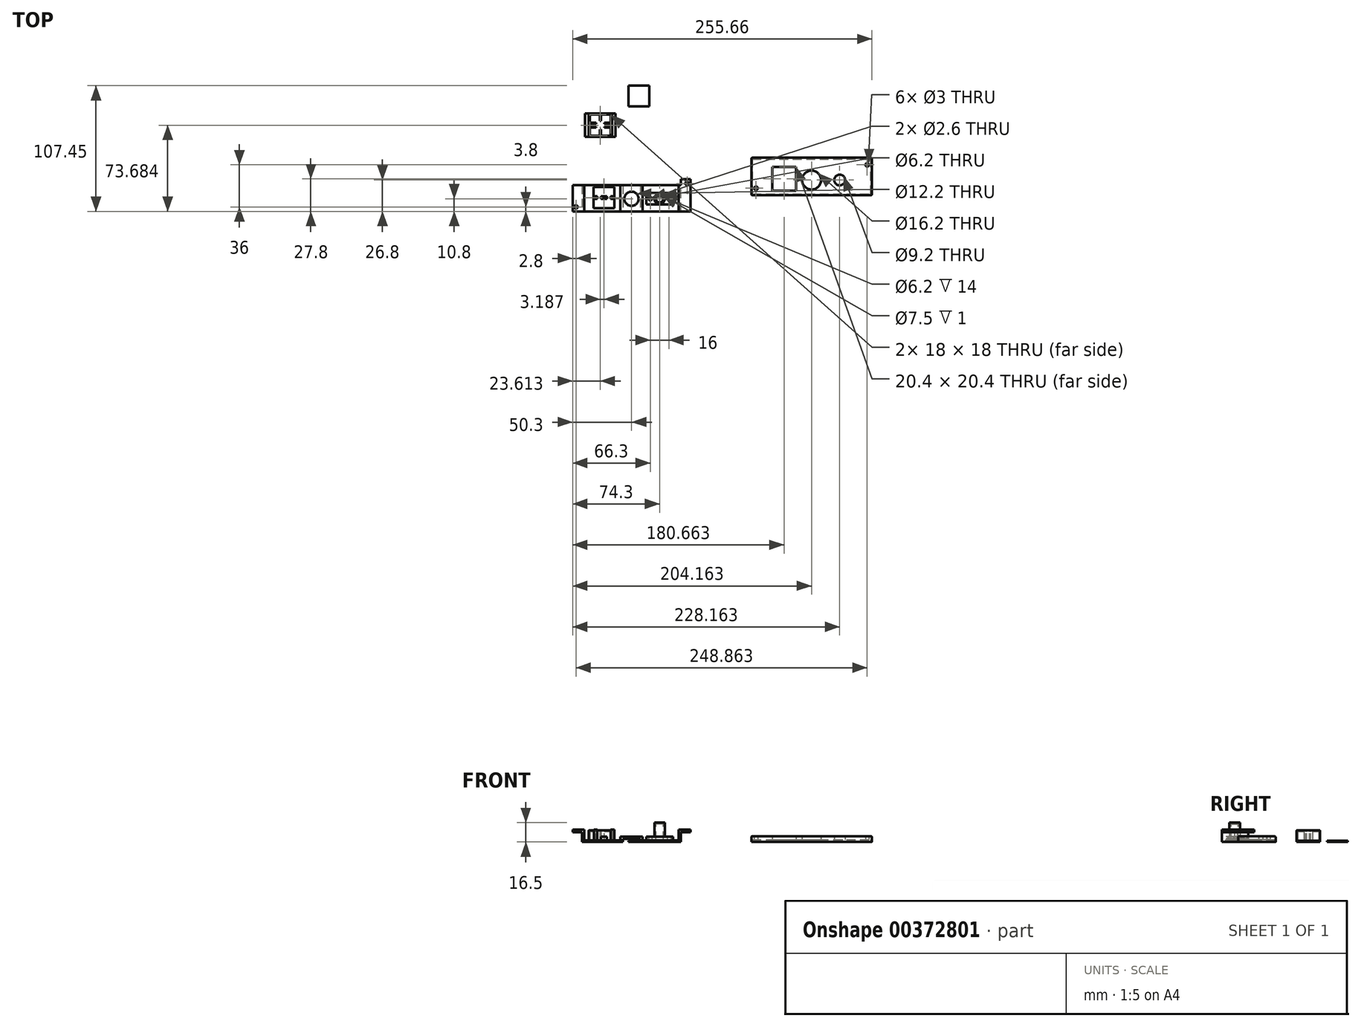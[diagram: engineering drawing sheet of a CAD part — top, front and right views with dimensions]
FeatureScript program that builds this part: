
annotation { "Feature Type Name" : "Feature", "Feature Type Description" : "" }
export const myFeature = defineFeature(function(context is Context, id is Id, definition is map)
    precondition{}
    {
        {
            var Q0;
            Q0=qCreatedBy(makeId("Top.planeOp"),FACE);
            var sketch = newSketch(context, id + "F0", { "sketchPlane" : qUnion([Q0])});
            skPoint(sketch, "E0.middle", {"position": v(0, 0) * mm});
            skCircle(sketch, "E1", {"center": v(-47.5, -10) * mm, "radius": 1.3 * mm, "construction": true});
            skCircle(sketch, "E2", {"center": v(47.5, 10) * mm, "radius": 1.3 * mm, "construction": true});
            skLineSegment(sketch, "E3.bottom", {"start": v(-32.5, 7) * mm, "end": v(-14.5, 7) * mm});
            skLineSegment(sketch, "E3.top", {"start": v(-32.5, -11) * mm, "end": v(-14.5, -11) * mm});
            skLineSegment(sketch, "E3.left", {"start": v(-32.5, 7) * mm, "end": v(-32.5, -1) * mm});
            skLineSegment(sketch, "E3.right", {"start": v(-14.5, 7) * mm, "end": v(-14.5, -11) * mm});
            skLineSegment(sketch, "E4.bottom", {"start": v(-29.25, 7) * mm, "end": v(-27.25, 7) * mm});
            skLineSegment(sketch, "E4.top", {"start": v(-29.25, -11) * mm, "end": v(-27.25, -11) * mm});
            skLineSegment(sketch, "E4.left", {"start": v(-29.25, 7) * mm, "end": v(-29.25, -1) * mm});
            skLineSegment(sketch, "E4.right", {"start": v(-27.25, 7) * mm, "end": v(-27.25, -1) * mm});
            skLineSegment(sketch, "E5.bottom", {"start": v(-19.75, 7) * mm, "end": v(-17.75, 7) * mm});
            skLineSegment(sketch, "E5.top", {"start": v(-19.75, -11) * mm, "end": v(-17.75, -11) * mm});
            skLineSegment(sketch, "E5.left", {"start": v(-19.75, 7) * mm, "end": v(-19.75, -1) * mm});
            skLineSegment(sketch, "E5.right", {"start": v(-17.75, 7) * mm, "end": v(-17.75, -1) * mm});
            skLineSegment(sketch, "E6.bottom", {"start": v(-32.5, -1) * mm, "end": v(-29.25, -1) * mm});
            skLineSegment(sketch, "E6.top", {"start": v(-32.5, -3) * mm, "end": v(-29.25, -3) * mm});
            skLineSegment(sketch, "E6.left", {"start": v(-32.5, -1) * mm, "end": v(-32.5, -3) * mm});
            skLineSegment(sketch, "E7.trimOffspring", {"start": v(-29.25, -3) * mm, "end": v(-29.25, -11) * mm});
            skLineSegment(sketch, "E8.trimOffspring", {"start": v(-27.25, -1) * mm, "end": v(-19.75, -1) * mm});
            skLineSegment(sketch, "E9.trimOffspring", {"start": v(-27.25, -3) * mm, "end": v(-27.25, -11) * mm});
            skLineSegment(sketch, "E10.trimOffspring", {"start": v(-27.25, -3) * mm, "end": v(-19.75, -3) * mm});
            skLineSegment(sketch, "E11.trimOffspring", {"start": v(-17.75, -1) * mm, "end": v(-14.5, -1) * mm});
            skLineSegment(sketch, "E12.trimOffspring", {"start": v(-17.75, -3) * mm, "end": v(-14.5, -3) * mm});
            skLineSegment(sketch, "E13.trimOffspring", {"start": v(-19.75, -3) * mm, "end": v(-19.75, -11) * mm});
            skLineSegment(sketch, "E14.trimOffspring", {"start": v(-17.75, -3) * mm, "end": v(-17.75, -11) * mm});
            skLineSegment(sketch, "E15.trimOffspring", {"start": v(-32.5, -3) * mm, "end": v(-32.5, -11) * mm});
            skCircle(sketch, "E16", {"center": v(24, -3) * mm, "radius": 3.1 * mm});
            skLineSegment(sketch, "E17.bottom", {"start": v(22.75, -10.5) * mm, "end": v(20.75, -10.5) * mm, "construction": true});
            skLineSegment(sketch, "E17.top", {"start": v(22.75, 4.5) * mm, "end": v(20.75, 4.5) * mm, "construction": true});
            skLineSegment(sketch, "E17.left", {"start": v(22.75, -10.5) * mm, "end": v(22.75, 4.5) * mm, "construction": true});
            skLineSegment(sketch, "E17.right", {"start": v(20.75, -10.5) * mm, "end": v(20.75, 4.5) * mm, "construction": true});
            skPoint(sketch, "E17.middle", {"position": v(21.75, -3) * mm});
            skLineSegment(sketch, "E18.bottom", {"start": v(25.25, -10.5) * mm, "end": v(27.25, -10.5) * mm, "construction": true});
            skLineSegment(sketch, "E18.top", {"start": v(25.25, 4.5) * mm, "end": v(27.25, 4.5) * mm, "construction": true});
            skLineSegment(sketch, "E18.left", {"start": v(25.25, -10.5) * mm, "end": v(25.25, 4.5) * mm, "construction": true});
            skLineSegment(sketch, "E18.right", {"start": v(27.25, -10.5) * mm, "end": v(27.25, 4.5) * mm, "construction": true});
            skPoint(sketch, "E18.middle", {"position": v(26.25, -3) * mm});
            skCircle(sketch, "E19", {"center": v(16, -3) * mm, "radius": 1.3 * mm});
            skPoint(sketch, "E19.centerSnap0", {"position": v(20.75, -3) * mm});
            skCircle(sketch, "E20", {"center": v(32, -3) * mm, "radius": 1.3 * mm});
            skPoint(sketch, "E20.centerSnap0", {"position": v(27.25, -3) * mm});
            skLineSegment(sketch, "E21.bottom", {"start": v(42.3, -13.8) * mm, "end": v(-42.3, -13.8) * mm});
            skLineSegment(sketch, "E21.top", {"start": v(42.3, 13.8) * mm, "end": v(-42.3, 13.8) * mm});
            skLineSegment(sketch, "E21.left", {"start": v(42.3, -13.8) * mm, "end": v(42.3, 13.8) * mm});
            skLineSegment(sketch, "E21.right", {"start": v(-42.3, -13.8) * mm, "end": v(-42.3, 13.8) * mm});
            skLineSegment(sketch, "E22.bottom", {"start": v(50.5, -15) * mm, "end": v(-50.5, -15) * mm, "construction": true});
            skLineSegment(sketch, "E22.top", {"start": v(50.5, 15) * mm, "end": v(-50.5, 15) * mm, "construction": true});
            skLineSegment(sketch, "E22.left", {"start": v(50.5, -15) * mm, "end": v(50.5, 15) * mm, "construction": true});
            skLineSegment(sketch, "E22.right", {"start": v(-50.5, -15) * mm, "end": v(-50.5, 15) * mm, "construction": true});
            skCircle(sketch, "E23", {"center": v(0, -3) * mm, "radius": 6.1 * mm, "construction": true});
            skSolve(sketch);
        }
        {
            var Q0;
            {var subQ9=sQuery(id+"F0.wireOp",EDGE,"E3.left");Q0=makeQuery(id+"F0.imprint","IMPRINT",FACE,{"disambiguationData":[TD([[makeQuery(id+"F0.imprint","IMPRINT",EDGE,{"derivedFrom":subQ9}),-1.0]])]});}
            var Q1;
            Q1=makeQuery(id+"F0.imprint","IMPRINT",FACE,{"disambiguationData":[TD([[makeQuery(id+"F0.imprint","IMPRINT",EDGE,{"derivedFrom":sQuery(id+"F0.wireOp",EDGE,"E4.bottom")}),-1.0]])]});
            extrude(context, id + "F1", {"entities" : qUnion([Q0, Q1]), "depth" : 1.5 * mm});
        }
        {
            var Q0;
            Q0=makeQuery(id+"F1.opExtrude","CAP_FACE",FACE,{"disambiguationData":[OSD([sQuery(id+"F0.wireOp",EDGE,"E1"),sQuery(id+"F0.wireOp",EDGE,"E2"),sQuery(id+"F0.wireOp",EDGE,"HjM1cqbq-AiCP-0QKJ-cJrE-Fvu34An3JJiY.bottom"),sQuery(id+"F0.wireOp",EDGE,"HjM1cqbq-AiCP-0QKJ-cJrE-Fvu34An3JJiY.top"),sQuery(id+"F0.wireOp",EDGE,"HjM1cqbq-AiCP-0QKJ-cJrE-Fvu34An3JJiY.left"),sQuery(id+"F0.wireOp",EDGE,"HjM1cqbq-AiCP-0QKJ-cJrE-Fvu34An3JJiY.right"),sQuery(id+"F0.wireOp",EDGE,"424KGZRB-5utR-a6Sk-f07y-1cyDiIB8TaRe"),sQuery(id+"F0.wireOp",EDGE,"xPdJMKwa-e6o6-zGCf-eMrl-vuys1Or93pA9"),sQuery(id+"F0.wireOp",EDGE,"E3.bottom"),sQuery(id+"F0.wireOp",EDGE,"E3.top"),sQuery(id+"F0.wireOp",EDGE,"E3.left"),sQuery(id+"F0.wireOp",EDGE,"E3.right"),sQuery(id+"F0.wireOp",EDGE,"E4.left"),sQuery(id+"F0.wireOp",EDGE,"E4.right"),sQuery(id+"F0.wireOp",EDGE,"E5.left"),sQuery(id+"F0.wireOp",EDGE,"E5.right"),sQuery(id+"F0.wireOp",EDGE,"E6.bottom"),sQuery(id+"F0.wireOp",EDGE,"E6.top"),sQuery(id+"F0.wireOp",EDGE,"E7.trimOffspring"),sQuery(id+"F0.wireOp",EDGE,"E8.trimOffspring"),sQuery(id+"F0.wireOp",EDGE,"E9.trimOffspring"),sQuery(id+"F0.wireOp",EDGE,"E10.trimOffspring"),sQuery(id+"F0.wireOp",EDGE,"E11.trimOffspring"),sQuery(id+"F0.wireOp",EDGE,"E12.trimOffspring"),sQuery(id+"F0.wireOp",EDGE,"E13.trimOffspring"),sQuery(id+"F0.wireOp",EDGE,"E14.trimOffspring"),sQuery(id+"F0.wireOp",EDGE,"E15.trimOffspring")])],"isStart":false});
            var sketch = newSketch(context, id + "F2", { "sketchPlane" : qUnion([Q0])});
            skLineSegment(sketch, "E24.bottom", {"start": v(-29.25, -1) * mm, "end": v(-32.25, -1) * mm});
            skLineSegment(sketch, "E24.top", {"start": v(-29.25, -3) * mm, "end": v(-32.25, -3) * mm});
            skLineSegment(sketch, "E24.left", {"start": v(-29.25, -1) * mm, "end": v(-29.25, -3) * mm});
            skLineSegment(sketch, "E24.right", {"start": v(-32.25, -1) * mm, "end": v(-32.25, -3) * mm});
            skLineSegment(sketch, "E25.bottom", {"start": v(-17.75, -1) * mm, "end": v(-14.75, -1) * mm});
            skLineSegment(sketch, "E25.top", {"start": v(-17.75, -3) * mm, "end": v(-14.75, -3) * mm});
            skLineSegment(sketch, "E25.left", {"start": v(-17.75, -1) * mm, "end": v(-17.75, -3) * mm});
            skLineSegment(sketch, "E25.right", {"start": v(-14.75, -1) * mm, "end": v(-14.75, -3) * mm});
            skSolve(sketch);
        }
        {
            var Q0;
            Q0=qSketchRegion(id+"F2",true);
            extrude(context, id + "F3", {"entities" : qUnion([Q0]), "operationType" : NewBodyOperationType.ADD, "depth" : 9 * mm});
        }
        {
            var Q0;
            Q0=qCreatedBy(makeId("Top.planeOp"),FACE);
            var sketch = newSketch(context, id + "F4", { "sketchPlane" : qUnion([Q0])});
            skLineSegment(sketch, "E26.bottom", {"start": v(-36.69, 69.88) * mm, "end": v(-16.69, 69.88) * mm});
            skLineSegment(sketch, "E26.top", {"start": v(-36.69, 49.88) * mm, "end": v(-16.69, 49.88) * mm});
            skLineSegment(sketch, "E26.left", {"start": v(-36.69, 69.88) * mm, "end": v(-36.69, 49.88) * mm});
            skLineSegment(sketch, "E26.right", {"start": v(-16.69, 69.88) * mm, "end": v(-16.69, 49.88) * mm});
            skLineSegment(sketch, "E27.bottom", {"start": v(-2.69, 93.65) * mm, "end": v(15.11, 93.65) * mm});
            skLineSegment(sketch, "E27.top", {"start": v(-2.69, 75.85) * mm, "end": v(15.11, 75.85) * mm});
            skLineSegment(sketch, "E27.left", {"start": v(-2.69, 93.65) * mm, "end": v(-2.69, 75.85) * mm});
            skLineSegment(sketch, "E27.right", {"start": v(15.11, 93.65) * mm, "end": v(15.11, 75.85) * mm});
            skSolve(sketch);
        }
        {
            var Q0;
            Q0=makeQuery(id+"F4.imprint","IMPRINT",FACE,{"disambiguationData":[TD([[makeQuery(id+"F4.imprint","IMPRINT",EDGE,{"derivedFrom":sQuery(id+"F4.wireOp",EDGE,"E26.bottom")}),-1.0]])]});
            extrude(context, id + "F5", {"entities" : qUnion([Q0]), "depth" : 10 * mm});
        }
        {
            var Q0;
            Q0=makeQuery(id+"F5.opExtrude","CAP_FACE",FACE,{"disambiguationData":[OSD([sQuery(id+"F4.wireOp",EDGE,"E26.bottom"),sQuery(id+"F4.wireOp",EDGE,"E26.top"),sQuery(id+"F4.wireOp",EDGE,"E26.left"),sQuery(id+"F4.wireOp",EDGE,"E26.right")])],"isStart":true});
            shell(context, id + "F6", {"entities" : qUnion([Q0]), "thickness" : 1 * mm});
        }
        {
            var Q0;
            Q0=makeQuery(id+"F5.opExtrude","CAP_FACE",FACE,{"disambiguationData":[OSD([sQuery(id+"F4.wireOp",EDGE,"E26.bottom"),sQuery(id+"F4.wireOp",EDGE,"E26.top"),sQuery(id+"F4.wireOp",EDGE,"E26.left"),sQuery(id+"F4.wireOp",EDGE,"E26.right")])],"isStart":true});
            var sketch = newSketch(context, id + "F7", { "sketchPlane" : qUnion([Q0])});
            skLineSegment(sketch, "E28.bottom", {"start": v(-35.69, -57.88) * mm, "end": v(-27.19, -57.88) * mm});
            skLineSegment(sketch, "E28.top", {"start": v(-35.69, -58.58) * mm, "end": v(-27.19, -58.58) * mm});
            skLineSegment(sketch, "E28.left", {"start": v(-35.69, -57.88) * mm, "end": v(-35.69, -58.58) * mm});
            skLineSegment(sketch, "E28.right", {"start": v(-17.69, -57.88) * mm, "end": v(-17.69, -58.58) * mm});
            skLineSegment(sketch, "E29.bottom", {"start": v(-35.69, -61.18) * mm, "end": v(-27.19, -61.18) * mm});
            skLineSegment(sketch, "E29.top", {"start": v(-35.69, -61.88) * mm, "end": v(-27.19, -61.88) * mm});
            skLineSegment(sketch, "E29.left", {"start": v(-35.69, -61.18) * mm, "end": v(-35.69, -61.88) * mm});
            skLineSegment(sketch, "E29.right", {"start": v(-17.69, -61.18) * mm, "end": v(-17.69, -61.88) * mm});
            skLineSegment(sketch, "E30.bottom", {"start": v(-27.19, -50.88) * mm, "end": v(-26.19, -50.88) * mm});
            skLineSegment(sketch, "E30.top", {"start": v(-27.19, -68.88) * mm, "end": v(-26.19, -68.88) * mm});
            skLineSegment(sketch, "E30.left", {"start": v(-27.19, -50.88) * mm, "end": v(-27.19, -68.88) * mm});
            skLineSegment(sketch, "E30.right", {"start": v(-26.19, -50.88) * mm, "end": v(-26.19, -68.88) * mm});
            skLineSegment(sketch, "E31.trimOffspring", {"start": v(-26.19, -57.88) * mm, "end": v(-17.69, -57.88) * mm});
            skLineSegment(sketch, "E32.trimOffspring", {"start": v(-26.19, -58.58) * mm, "end": v(-17.69, -58.58) * mm});
            skLineSegment(sketch, "E33.trimOffspring", {"start": v(-26.19, -61.18) * mm, "end": v(-17.69, -61.18) * mm});
            skLineSegment(sketch, "E34.trimOffspring", {"start": v(-26.19, -61.88) * mm, "end": v(-17.69, -61.88) * mm});
            skSolve(sketch);
        }
        {
            var Q0;
            Q0=qSketchRegion(id+"F7",true);
            extrude(context, id + "F8", {"entities" : qUnion([Q0]), "operationType" : NewBodyOperationType.ADD, "oppositeDirection" : true, "depth" : 9 * mm});
        }
        {
            var Q0;
            Q0=makeQuery(id+"F8.boolean.opBoolean","MERGE",FACE,{"derivedFrom":[makeQuery(id+"F5.opExtrude","CAP_FACE",FACE,{"disambiguationData":[OSD([sQuery(id+"F4.wireOp",EDGE,"E26.bottom"),sQuery(id+"F4.wireOp",EDGE,"E26.top"),sQuery(id+"F4.wireOp",EDGE,"E26.left"),sQuery(id+"F4.wireOp",EDGE,"E26.right")])],"isStart":true}),makeQuery(id+"F8.opExtrude","CAP_FACE",FACE,{"disambiguationData":[OSD([sQuery(id+"F7.wireOp",EDGE,"E28.bottom"),sQuery(id+"F7.wireOp",EDGE,"E28.top"),sQuery(id+"F7.wireOp",EDGE,"E28.left"),sQuery(id+"F7.wireOp",EDGE,"E28.right"),sQuery(id+"F7.wireOp",EDGE,"E29.bottom"),sQuery(id+"F7.wireOp",EDGE,"E29.top"),sQuery(id+"F7.wireOp",EDGE,"E29.left"),sQuery(id+"F7.wireOp",EDGE,"E29.right"),sQuery(id+"F7.wireOp",EDGE,"E30.bottom"),sQuery(id+"F7.wireOp",EDGE,"E30.top"),sQuery(id+"F7.wireOp",EDGE,"E30.left"),sQuery(id+"F7.wireOp",EDGE,"E30.right"),sQuery(id+"F7.wireOp",EDGE,"E31.trimOffspring"),sQuery(id+"F7.wireOp",EDGE,"E32.trimOffspring"),sQuery(id+"F7.wireOp",EDGE,"E33.trimOffspring"),sQuery(id+"F7.wireOp",EDGE,"E34.trimOffspring")])],"isStart":true})]});
            var sketch = newSketch(context, id + "F9", { "sketchPlane" : qUnion([Q0])});
            skLineSegment(sketch, "E35.bottom", {"start": v(-30.29, -56.28) * mm, "end": v(-23.09, -56.28) * mm});
            skLineSegment(sketch, "E35.top", {"start": v(-30.29, -63.48) * mm, "end": v(-23.09, -63.48) * mm});
            skLineSegment(sketch, "E35.left", {"start": v(-30.29, -56.28) * mm, "end": v(-30.29, -63.48) * mm});
            skLineSegment(sketch, "E35.right", {"start": v(-23.09, -56.28) * mm, "end": v(-23.09, -63.48) * mm});
            skSolve(sketch);
        }
        {
            var Q0;
            Q0=qSketchRegion(id+"F9",true);
            extrude(context, id + "F10", {"entities" : qUnion([Q0]), "operationType" : NewBodyOperationType.REMOVE, "oppositeDirection" : true, "depth" : 9 * mm});
        }
        {
            var Q0;
            Q0=makeQuery(id+"F8.boolean.opBoolean","MERGE",FACE,{"derivedFrom":[makeQuery(id+"F5.opExtrude","CAP_FACE",FACE,{"disambiguationData":[OSD([sQuery(id+"F4.wireOp",EDGE,"E26.bottom"),sQuery(id+"F4.wireOp",EDGE,"E26.top"),sQuery(id+"F4.wireOp",EDGE,"E26.left"),sQuery(id+"F4.wireOp",EDGE,"E26.right")])],"isStart":true}),makeQuery(id+"F8.opExtrude","CAP_FACE",FACE,{"disambiguationData":[OSD([sQuery(id+"F7.wireOp",EDGE,"E28.bottom"),sQuery(id+"F7.wireOp",EDGE,"E28.top"),sQuery(id+"F7.wireOp",EDGE,"E28.left"),sQuery(id+"F7.wireOp",EDGE,"E28.right"),sQuery(id+"F7.wireOp",EDGE,"E29.bottom"),sQuery(id+"F7.wireOp",EDGE,"E29.top"),sQuery(id+"F7.wireOp",EDGE,"E29.left"),sQuery(id+"F7.wireOp",EDGE,"E29.right"),sQuery(id+"F7.wireOp",EDGE,"E30.bottom"),sQuery(id+"F7.wireOp",EDGE,"E30.top"),sQuery(id+"F7.wireOp",EDGE,"E30.left"),sQuery(id+"F7.wireOp",EDGE,"E30.right"),sQuery(id+"F7.wireOp",EDGE,"E31.trimOffspring"),sQuery(id+"F7.wireOp",EDGE,"E32.trimOffspring"),sQuery(id+"F7.wireOp",EDGE,"E33.trimOffspring"),sQuery(id+"F7.wireOp",EDGE,"E34.trimOffspring")])],"isStart":true})]});
            var sketch = newSketch(context, id + "F11", { "sketchPlane" : qUnion([Q0])});
            skLineSegment(sketch, "E36.bottom", {"start": v(-16.69, -69.88) * mm, "end": v(-13.69, -69.88) * mm});
            skLineSegment(sketch, "E36.top", {"start": v(-16.69, -49.88) * mm, "end": v(-13.69, -49.88) * mm});
            skLineSegment(sketch, "E36.left", {"start": v(-16.69, -69.88) * mm, "end": v(-16.69, -49.88) * mm});
            skLineSegment(sketch, "E36.right", {"start": v(-13.69, -69.88) * mm, "end": v(-13.69, -49.88) * mm});
            skLineSegment(sketch, "E37.bottom", {"start": v(-36.69, -69.88) * mm, "end": v(-39.69, -69.88) * mm});
            skLineSegment(sketch, "E37.top", {"start": v(-36.69, -49.88) * mm, "end": v(-39.69, -49.88) * mm});
            skLineSegment(sketch, "E37.left", {"start": v(-36.69, -69.88) * mm, "end": v(-36.69, -49.88) * mm});
            skLineSegment(sketch, "E37.right", {"start": v(-39.69, -69.88) * mm, "end": v(-39.69, -49.88) * mm});
            skSolve(sketch);
        }
        {
            var Q0;
            Q0=makeQuery(id+"F11.imprint","IMPRINT",FACE,{"disambiguationData":[TD([[makeQuery(id+"F11.imprint","IMPRINT",EDGE,{"derivedFrom":sQuery(id+"F11.wireOp",EDGE,"E37.bottom")}),-1.0]])]});
            var Q1;
            Q1=makeQuery(id+"F11.imprint","IMPRINT",FACE,{"disambiguationData":[TD([[makeQuery(id+"F11.imprint","IMPRINT",EDGE,{"derivedFrom":sQuery(id+"F11.wireOp",EDGE,"E36.bottom")}),1.0]])]});
            extrude(context, id + "F12", {"entities" : qUnion([Q0, Q1]), "operationType" : NewBodyOperationType.ADD, "oppositeDirection" : true, "depth" : 1 * mm});
        }
        {
            var Q0;
            Q0=makeQuery(id+"F5.opExtrude","CAP_FACE",FACE,{"disambiguationData":[OSD([sQuery(id+"F4.wireOp",EDGE,"E26.bottom"),sQuery(id+"F4.wireOp",EDGE,"E26.top"),sQuery(id+"F4.wireOp",EDGE,"E26.left"),sQuery(id+"F4.wireOp",EDGE,"E26.right")])],"isStart":false});
            var sketch = newSketch(context, id + "F13", { "sketchPlane" : qUnion([Q0])});
            skLineSegment(sketch, "E38.bottom", {"start": v(-35.69, 68.88) * mm, "end": v(-17.69, 68.88) * mm});
            skLineSegment(sketch, "E38.top", {"start": v(-35.69, 50.88) * mm, "end": v(-17.69, 50.88) * mm});
            skLineSegment(sketch, "E38.left", {"start": v(-35.69, 68.88) * mm, "end": v(-35.69, 50.88) * mm});
            skLineSegment(sketch, "E38.right", {"start": v(-17.69, 68.88) * mm, "end": v(-17.69, 50.88) * mm});
            skSolve(sketch);
        }
        {
            var Q0;
            Q0=qSketchRegion(id+"F13",true);
            extrude(context, id + "F14", {"entities" : qUnion([Q0]), "operationType" : NewBodyOperationType.REMOVE, "oppositeDirection" : true, "depth" : 1 * mm});
        }
        {
            var Q0;
            Q0=makeQuery(id+"F5.opExtrude","SWEPT_EDGE",EDGE,{"disambiguationData":[OSD([sQuery(id+"F4.wireOp",EDGE,"E26.top"),sQuery(id+"F4.wireOp",EDGE,"E26.right")])]});
            var Q1;
            Q1=makeQuery(id+"F5.opExtrude","SWEPT_EDGE",EDGE,{"disambiguationData":[OSD([sQuery(id+"F4.wireOp",EDGE,"E26.bottom"),sQuery(id+"F4.wireOp",EDGE,"E26.right")])]});
            var Q2;
            Q2=makeQuery(id+"F5.opExtrude","CAP_EDGE",EDGE,{"disambiguationData":[OSD([sQuery(id+"F4.wireOp",EDGE,"E26.right")])],"isStart":false});
            var Q3;
            Q3=makeQuery(id+"F5.opExtrude","CAP_EDGE",EDGE,{"disambiguationData":[OSD([sQuery(id+"F4.wireOp",EDGE,"E26.bottom")])],"isStart":false});
            var Q4;
            Q4=makeQuery(id+"F5.opExtrude","CAP_EDGE",EDGE,{"disambiguationData":[OSD([sQuery(id+"F4.wireOp",EDGE,"E26.top")])],"isStart":false});
            var Q5;
            Q5=makeQuery(id+"F5.opExtrude","CAP_EDGE",EDGE,{"disambiguationData":[OSD([sQuery(id+"F4.wireOp",EDGE,"E26.left")])],"isStart":false});
            var Q6;
            Q6=makeQuery(id+"F5.opExtrude","SWEPT_EDGE",EDGE,{"disambiguationData":[OSD([sQuery(id+"F4.wireOp",EDGE,"E26.top"),sQuery(id+"F4.wireOp",EDGE,"E26.left")])]});
            var Q7;
            Q7=makeQuery(id+"F5.opExtrude","SWEPT_EDGE",EDGE,{"disambiguationData":[OSD([sQuery(id+"F4.wireOp",EDGE,"E26.bottom"),sQuery(id+"F4.wireOp",EDGE,"E26.left")])]});
            fillet(context, id + "F15", {"entities" : qUnion([Q0, Q1, Q2, Q3, Q4, Q5, Q6, Q7]), "radius" : 0.5 * mm, "tangentPropagation" : true, "allowEdgeOverflow" : false});
        }
        {
            var Q0;
            Q0=makeQuery(id+"F4.imprint","IMPRINT",FACE,{"disambiguationData":[TD([[makeQuery(id+"F4.imprint","IMPRINT",EDGE,{"derivedFrom":sQuery(id+"F4.wireOp",EDGE,"E27.bottom")}),-1.0]])]});
            extrude(context, id + "F16", {"entities" : qUnion([Q0]), "depth" : 1 * mm});
        }
        {
            var Q0;
            Q0=makeQuery(id+"F1.opExtrude","CAP_FACE",FACE,{"disambiguationData":[OSD([sQuery(id+"F0.wireOp",EDGE,"E1"),sQuery(id+"F0.wireOp",EDGE,"E2"),sQuery(id+"F0.wireOp",EDGE,"HjM1cqbq-AiCP-0QKJ-cJrE-Fvu34An3JJiY.bottom"),sQuery(id+"F0.wireOp",EDGE,"HjM1cqbq-AiCP-0QKJ-cJrE-Fvu34An3JJiY.top"),sQuery(id+"F0.wireOp",EDGE,"HjM1cqbq-AiCP-0QKJ-cJrE-Fvu34An3JJiY.left"),sQuery(id+"F0.wireOp",EDGE,"HjM1cqbq-AiCP-0QKJ-cJrE-Fvu34An3JJiY.right"),sQuery(id+"F0.wireOp",EDGE,"424KGZRB-5utR-a6Sk-f07y-1cyDiIB8TaRe"),sQuery(id+"F0.wireOp",EDGE,"xPdJMKwa-e6o6-zGCf-eMrl-vuys1Or93pA9"),sQuery(id+"F0.wireOp",EDGE,"E3.bottom"),sQuery(id+"F0.wireOp",EDGE,"E3.top"),sQuery(id+"F0.wireOp",EDGE,"E3.left"),sQuery(id+"F0.wireOp",EDGE,"E3.right"),sQuery(id+"F0.wireOp",EDGE,"E4.left"),sQuery(id+"F0.wireOp",EDGE,"E4.right"),sQuery(id+"F0.wireOp",EDGE,"E5.left"),sQuery(id+"F0.wireOp",EDGE,"E5.right"),sQuery(id+"F0.wireOp",EDGE,"E6.bottom"),sQuery(id+"F0.wireOp",EDGE,"E6.top"),sQuery(id+"F0.wireOp",EDGE,"E7.trimOffspring"),sQuery(id+"F0.wireOp",EDGE,"E8.trimOffspring"),sQuery(id+"F0.wireOp",EDGE,"E9.trimOffspring"),sQuery(id+"F0.wireOp",EDGE,"E10.trimOffspring"),sQuery(id+"F0.wireOp",EDGE,"E11.trimOffspring"),sQuery(id+"F0.wireOp",EDGE,"E12.trimOffspring"),sQuery(id+"F0.wireOp",EDGE,"E13.trimOffspring"),sQuery(id+"F0.wireOp",EDGE,"E14.trimOffspring"),sQuery(id+"F0.wireOp",EDGE,"E15.trimOffspring")])],"isStart":false});
            var sketch = newSketch(context, id + "F17", { "sketchPlane" : qUnion([Q0])});
            skLineSegment(sketch, "E39.bottom", {"start": v(-26, -1) * mm, "end": v(-21, -1) * mm});
            skLineSegment(sketch, "E39.top", {"start": v(-26, -3) * mm, "end": v(-21, -3) * mm});
            skLineSegment(sketch, "E39.left", {"start": v(-26, -1) * mm, "end": v(-26, -3) * mm});
            skLineSegment(sketch, "E39.right", {"start": v(-21, -1) * mm, "end": v(-21, -3) * mm});
            skSolve(sketch);
        }
        {
            var Q0;
            Q0=qSketchRegion(id+"F17",true);
            extrude(context, id + "F18", {"entities" : qUnion([Q0]), "operationType" : NewBodyOperationType.ADD, "depth" : 3 * mm});
        }
        {
            var Q0;
            Q0=qCreatedBy(makeId("Top.planeOp"),FACE);
            var sketch = newSketch(context, id + "F19", { "sketchPlane" : qUnion([Q0])});
            skLineSegment(sketch, "E40.bottom", {"start": v(103.36, 32) * mm, "end": v(204.36, 32) * mm, "construction": true});
            skLineSegment(sketch, "E40.top", {"start": v(103.36, 0) * mm, "end": v(204.36, 0) * mm, "construction": true});
            skLineSegment(sketch, "E40.left", {"start": v(103.36, 32) * mm, "end": v(103.36, 0) * mm, "construction": true});
            skLineSegment(sketch, "E40.right", {"start": v(204.36, 32) * mm, "end": v(204.36, 0) * mm, "construction": true});
            skLineSegment(sketch, "E41.bottom", {"start": v(102.36, 32) * mm, "end": v(205.36, 32) * mm});
            skLineSegment(sketch, "E41.top", {"start": v(102.36, 0) * mm, "end": v(205.36, 0) * mm});
            skLineSegment(sketch, "E41.left", {"start": v(102.36, 32) * mm, "end": v(102.36, 0) * mm});
            skLineSegment(sketch, "E41.right", {"start": v(205.36, 32) * mm, "end": v(205.36, 0) * mm});
            skCircle(sketch, "E42", {"center": v(106.36, 6) * mm, "radius": 1.5 * mm});
            skCircle(sketch, "E43", {"center": v(201.36, 26) * mm, "radius": 1.5 * mm});
            skCircle(sketch, "E44", {"center": v(153.86, 13) * mm, "radius": 8.1 * mm});
            skCircle(sketch, "E45", {"center": v(177.86, 13) * mm, "radius": 4.6 * mm});
            skLineSegment(sketch, "E46.bottom", {"start": v(140.56, 3.8) * mm, "end": v(120.16, 3.8) * mm});
            skLineSegment(sketch, "E46.top", {"start": v(140.56, 24.2) * mm, "end": v(120.16, 24.2) * mm});
            skLineSegment(sketch, "E46.left", {"start": v(140.56, 3.8) * mm, "end": v(140.56, 24.2) * mm});
            skLineSegment(sketch, "E46.right", {"start": v(120.16, 3.8) * mm, "end": v(120.16, 24.2) * mm});
            skPoint(sketch, "E46.middle", {"position": v(130.36, 14) * mm});
            skSolve(sketch);
        }
        {
            var Q0;
            Q0=qSketchRegion(id+"F19",true);
            extrude(context, id + "F20", {"entities" : qUnion([Q0]), "depth" : 5 * mm});
        }
        {
            var Q0;
            Q0=makeQuery(id+"F20.opExtrude","CAP_FACE",FACE,{"disambiguationData":[OSD([sQuery(id+"F19.wireOp",EDGE,"E41.bottom"),sQuery(id+"F19.wireOp",EDGE,"E41.top"),sQuery(id+"F19.wireOp",EDGE,"E41.left"),sQuery(id+"F19.wireOp",EDGE,"E41.right"),sQuery(id+"F19.wireOp",EDGE,"E42"),sQuery(id+"F19.wireOp",EDGE,"E43"),sQuery(id+"F19.wireOp",EDGE,"RyGLUrYX-1u43-e16M-MsOJ-A2O3aQofN9jR.bottom"),sQuery(id+"F19.wireOp",EDGE,"RyGLUrYX-1u43-e16M-MsOJ-A2O3aQofN9jR.top"),sQuery(id+"F19.wireOp",EDGE,"RyGLUrYX-1u43-e16M-MsOJ-A2O3aQofN9jR.left"),sQuery(id+"F19.wireOp",EDGE,"RyGLUrYX-1u43-e16M-MsOJ-A2O3aQofN9jR.right")])],"isStart":true});
            var sketch = newSketch(context, id + "F21", { "sketchPlane" : qUnion([Q0])});
            skLineSegment(sketch, "E47.bottom", {"start": v(103.36, -1) * mm, "end": v(204.36, -1) * mm});
            skLineSegment(sketch, "E47.top", {"start": v(103.36, -31) * mm, "end": v(204.36, -31) * mm});
            skLineSegment(sketch, "E47.left", {"start": v(103.36, -1) * mm, "end": v(103.36, -31) * mm});
            skLineSegment(sketch, "E47.right", {"start": v(204.36, -1) * mm, "end": v(204.36, -31) * mm});
            skSolve(sketch);
        }
        {
            var Q0;
            Q0=qSketchRegion(id+"F21",true);
            extrude(context, id + "F22", {"entities" : qUnion([Q0]), "operationType" : NewBodyOperationType.REMOVE, "oppositeDirection" : true, "depth" : 2 * mm});
        }
        {
            var Q0;
            Q0=makeQuery(id+"F20.opExtrude","CAP_EDGE",EDGE,{"disambiguationData":[OSD([sQuery(id+"F19.wireOp",EDGE,"E41.left")])],"isStart":false});
            var Q1;
            Q1=makeQuery(id+"F20.opExtrude","CAP_EDGE",EDGE,{"disambiguationData":[OSD([sQuery(id+"F19.wireOp",EDGE,"E41.bottom")])],"isStart":false});
            var Q2;
            Q2=makeQuery(id+"F20.opExtrude","CAP_EDGE",EDGE,{"disambiguationData":[OSD([sQuery(id+"F19.wireOp",EDGE,"E41.top")])],"isStart":false});
            var Q3;
            Q3=makeQuery(id+"F20.opExtrude","CAP_EDGE",EDGE,{"disambiguationData":[OSD([sQuery(id+"F19.wireOp",EDGE,"E41.right")])],"isStart":false});
            var Q4;
            Q4=makeQuery(id+"F20.opExtrude","SWEPT_EDGE",EDGE,{"disambiguationData":[OSD([sQuery(id+"F19.wireOp",EDGE,"E41.bottom"),sQuery(id+"F19.wireOp",EDGE,"E41.right")])]});
            var Q5;
            Q5=makeQuery(id+"F20.opExtrude","SWEPT_EDGE",EDGE,{"disambiguationData":[OSD([sQuery(id+"F19.wireOp",EDGE,"E41.top"),sQuery(id+"F19.wireOp",EDGE,"E41.right")])]});
            var Q6;
            Q6=makeQuery(id+"F20.opExtrude","SWEPT_EDGE",EDGE,{"disambiguationData":[OSD([sQuery(id+"F19.wireOp",EDGE,"E41.bottom"),sQuery(id+"F19.wireOp",EDGE,"E41.left")])]});
            var Q7;
            Q7=makeQuery(id+"F20.opExtrude","SWEPT_EDGE",EDGE,{"disambiguationData":[OSD([sQuery(id+"F19.wireOp",EDGE,"E41.top"),sQuery(id+"F19.wireOp",EDGE,"E41.left")])]});
            fillet(context, id + "F23", {"entities" : qUnion([Q0, Q1, Q2, Q3, Q4, Q5, Q6, Q7]), "radius" : 1 * mm, "tangentPropagation" : true, "allowEdgeOverflow" : false});
        }
        {
            var Q0;
            Q0=makeQuery(id+"F1.opExtrude","SWEPT_FACE",FACE,{"disambiguationData":[OSD([sQuery(id+"F0.wireOp",EDGE,"E21.bottom")])]});
            var sketch = newSketch(context, id + "F24", { "sketchPlane" : qUnion([Q0])});
            skLineSegment(sketch, "E48.bottom", {"start": v(-42.3, 1.5) * mm, "end": v(-40.3, 1.5) * mm});
            skLineSegment(sketch, "E48.left", {"start": v(-42.3, 1.5) * mm, "end": v(-42.3, 8.5) * mm});
            skLineSegment(sketch, "E48.right", {"start": v(-40.3, 1.5) * mm, "end": v(-40.3, 10.5) * mm});
            skLineSegment(sketch, "E49.bottom", {"start": v(-40.3, 10.5) * mm, "end": v(-50.3, 10.5) * mm});
            skLineSegment(sketch, "E49.top", {"start": v(-42.3, 8.5) * mm, "end": v(-50.3, 8.5) * mm});
            skLineSegment(sketch, "E49.right", {"start": v(-50.3, 10.5) * mm, "end": v(-50.3, 8.5) * mm});
            skLineSegment(sketch, "E50", {"start": v(0, 8.22) * mm, "end": v(0, -6.23) * mm, "construction": true});
            skPoint(sketch, "E50.endSnap0", {"position": v(0, 1.5) * mm});
            skLineSegment(sketch, "E51.MirrorCS", {"start": v(42.3, 10.5) * mm, "end": v(40.3, 10.5) * mm});
            skLineSegment(sketch, "E52.MirrorCS", {"start": v(42.3, 10.5) * mm, "end": v(42.3, 8.5) * mm});
            skLineSegment(sketch, "E53.MirrorCS", {"start": v(42.3, 1.5) * mm, "end": v(40.3, 1.5) * mm});
            skLineSegment(sketch, "E54.MirrorCS", {"start": v(40.3, 1.5) * mm, "end": v(40.3, 10.5) * mm});
            skLineSegment(sketch, "E55.MirrorCS", {"start": v(50.3, 10.5) * mm, "end": v(50.3, 8.5) * mm});
            skLineSegment(sketch, "E56.MirrorCS", {"start": v(42.3, 1.5) * mm, "end": v(42.3, 10.5) * mm});
            skLineSegment(sketch, "E57.MirrorCS", {"start": v(42.3, 10.5) * mm, "end": v(50.3, 10.5) * mm});
            skLineSegment(sketch, "E58.MirrorCS", {"start": v(42.3, 8.5) * mm, "end": v(50.3, 8.5) * mm});
            skSolve(sketch);
        }
        {
            var Q0;
            Q0=qSketchRegion(id+"F24",true);
            extrude(context, id + "F25", {"entities" : qUnion([Q0]), "operationType" : NewBodyOperationType.ADD, "oppositeDirection" : true, "depth" : 27.6 * mm});
        }
        {
            var Q0;
            Q0=sQuery(id+"F0.wireOp",VERTEX,"E1.center");
            var Q1;
            Q1=sQuery(id+"F0.wireOp",VERTEX,"E2.center");
            var Q2;
            Q2=makeQuery(id+"F1.opExtrude","SWEPT_BODY",BODY,{"disambiguationData":[OSD([sQuery(id+"F0.wireOp",EDGE,"E3.bottom"),sQuery(id+"F0.wireOp",EDGE,"E3.top"),sQuery(id+"F0.wireOp",EDGE,"E3.left"),sQuery(id+"F0.wireOp",EDGE,"E3.right"),sQuery(id+"F0.wireOp",EDGE,"E4.left"),sQuery(id+"F0.wireOp",EDGE,"E4.right"),sQuery(id+"F0.wireOp",EDGE,"E5.left"),sQuery(id+"F0.wireOp",EDGE,"E5.right"),sQuery(id+"F0.wireOp",EDGE,"E6.bottom"),sQuery(id+"F0.wireOp",EDGE,"E6.top"),sQuery(id+"F0.wireOp",EDGE,"E7.trimOffspring"),sQuery(id+"F0.wireOp",EDGE,"E8.trimOffspring"),sQuery(id+"F0.wireOp",EDGE,"E9.trimOffspring"),sQuery(id+"F0.wireOp",EDGE,"E10.trimOffspring"),sQuery(id+"F0.wireOp",EDGE,"E11.trimOffspring"),sQuery(id+"F0.wireOp",EDGE,"E12.trimOffspring"),sQuery(id+"F0.wireOp",EDGE,"E13.trimOffspring"),sQuery(id+"F0.wireOp",EDGE,"E14.trimOffspring"),sQuery(id+"F0.wireOp",EDGE,"E15.trimOffspring"),sQuery(id+"F0.wireOp",EDGE,"E17.bottom"),sQuery(id+"F0.wireOp",EDGE,"E17.top"),sQuery(id+"F0.wireOp",EDGE,"E17.left"),sQuery(id+"F0.wireOp",EDGE,"E17.right"),sQuery(id+"F0.wireOp",EDGE,"E18.bottom"),sQuery(id+"F0.wireOp",EDGE,"E18.top"),sQuery(id+"F0.wireOp",EDGE,"E18.left"),sQuery(id+"F0.wireOp",EDGE,"E18.right"),sQuery(id+"F0.wireOp",EDGE,"E19"),sQuery(id+"F0.wireOp",EDGE,"E20"),sQuery(id+"F0.wireOp",EDGE,"E21.bottom"),sQuery(id+"F0.wireOp",EDGE,"E21.top"),sQuery(id+"F0.wireOp",EDGE,"E21.left"),sQuery(id+"F0.wireOp",EDGE,"E21.right"),sQuery(id+"F0.wireOp",EDGE,"P8dx2Xio-yyFz-oP8E-liUG-BQfSMQLC5rHF")])]});
            hole(context, id + "F26", {"style" : HoleStyle.SIMPLE, "endStyle" : HoleEndStyle.BLIND, "oppositeDirection" : true, "holeDiameter" : 3 * mm, "holeDepth" : 5 * mm, "tappedDepth" : 12 * mm, "tapClearance" : 3, "locations" : qUnion([Q0, Q1]), "scope" : qUnion([Q2])});
        }
        {
            var Q0;
            Q0=makeQuery(id+"F1.opExtrude","CAP_FACE",FACE,{"disambiguationData":[OSD([sQuery(id+"F0.wireOp",EDGE,"E3.bottom"),sQuery(id+"F0.wireOp",EDGE,"E3.top"),sQuery(id+"F0.wireOp",EDGE,"E3.left"),sQuery(id+"F0.wireOp",EDGE,"E3.right"),sQuery(id+"F0.wireOp",EDGE,"E4.left"),sQuery(id+"F0.wireOp",EDGE,"E4.right"),sQuery(id+"F0.wireOp",EDGE,"E5.left"),sQuery(id+"F0.wireOp",EDGE,"E5.right"),sQuery(id+"F0.wireOp",EDGE,"E6.bottom"),sQuery(id+"F0.wireOp",EDGE,"E6.top"),sQuery(id+"F0.wireOp",EDGE,"E7.trimOffspring"),sQuery(id+"F0.wireOp",EDGE,"E8.trimOffspring"),sQuery(id+"F0.wireOp",EDGE,"E9.trimOffspring"),sQuery(id+"F0.wireOp",EDGE,"E10.trimOffspring"),sQuery(id+"F0.wireOp",EDGE,"E11.trimOffspring"),sQuery(id+"F0.wireOp",EDGE,"E12.trimOffspring"),sQuery(id+"F0.wireOp",EDGE,"E13.trimOffspring"),sQuery(id+"F0.wireOp",EDGE,"E14.trimOffspring"),sQuery(id+"F0.wireOp",EDGE,"E15.trimOffspring"),sQuery(id+"F0.wireOp",EDGE,"E17.bottom"),sQuery(id+"F0.wireOp",EDGE,"E17.top"),sQuery(id+"F0.wireOp",EDGE,"E17.left"),sQuery(id+"F0.wireOp",EDGE,"E17.right"),sQuery(id+"F0.wireOp",EDGE,"E18.bottom"),sQuery(id+"F0.wireOp",EDGE,"E18.top"),sQuery(id+"F0.wireOp",EDGE,"E18.left"),sQuery(id+"F0.wireOp",EDGE,"E18.right"),sQuery(id+"F0.wireOp",EDGE,"E19"),sQuery(id+"F0.wireOp",EDGE,"E20"),sQuery(id+"F0.wireOp",EDGE,"E21.bottom"),sQuery(id+"F0.wireOp",EDGE,"E21.top"),sQuery(id+"F0.wireOp",EDGE,"E21.left"),sQuery(id+"F0.wireOp",EDGE,"E21.right"),sQuery(id+"F0.wireOp",EDGE,"P8dx2Xio-yyFz-oP8E-liUG-BQfSMQLC5rHF")])],"isStart":false});
            var sketch = newSketch(context, id + "F27", { "sketchPlane" : qUnion([Q0])});
            skLineSegment(sketch, "E59.bottom", {"start": v(35.5, -8) * mm, "end": v(12.5, -8) * mm});
            skLineSegment(sketch, "E59.top", {"start": v(35.5, 2) * mm, "end": v(12.5, 2) * mm});
            skLineSegment(sketch, "E59.left", {"start": v(35.5, -8) * mm, "end": v(35.5, 2) * mm});
            skLineSegment(sketch, "E59.right", {"start": v(12.5, -8) * mm, "end": v(12.5, 2) * mm});
            skPoint(sketch, "E59.middle", {"position": v(24, -3) * mm});
            skCircle(sketch, "E60", {"center": v(16, -3) * mm, "radius": 1.5 * mm});
            skCircle(sketch, "E61", {"center": v(32, -3) * mm, "radius": 1.5 * mm});
            skSolve(sketch);
        }
        {
            var Q0;
            Q0=qSketchRegion(id+"F27",true);
            extrude(context, id + "F28", {"entities" : qUnion([Q0]), "depth" : 3 * mm});
        }
        {
            var Q0;
            Q0=makeQuery(id+"F28.opExtrude","CAP_FACE",FACE,{"disambiguationData":[OSD([sQuery(id+"F27.wireOp",EDGE,"E59.bottom"),sQuery(id+"F27.wireOp",EDGE,"E59.top"),sQuery(id+"F27.wireOp",EDGE,"E59.left"),sQuery(id+"F27.wireOp",EDGE,"E59.right"),sQuery(id+"F27.wireOp",EDGE,"E60"),sQuery(id+"F27.wireOp",EDGE,"E61")])],"isStart":false});
            var sketch = newSketch(context, id + "F29", { "sketchPlane" : qUnion([Q0])});
            skCircle(sketch, "E62", {"center": v(24, -3) * mm, "radius": 4.5 * mm});
            skPoint(sketch, "E62.centerSnap0", {"position": v(24, 2) * mm});
            skPoint(sketch, "E62.centerSnap1", {"position": v(35.5, -3) * mm});
            skSolve(sketch);
        }
        {
            var Q0;
            Q0=qSketchRegion(id+"F29",true);
            extrude(context, id + "F30", {"entities" : qUnion([Q0]), "operationType" : NewBodyOperationType.ADD, "depth" : 12 * mm});
        }
        {
            var Q0;
            Q0=makeQuery(id+"F30.opExtrude","CAP_FACE",FACE,{"disambiguationData":[OSD([sQuery(id+"F29.wireOp",EDGE,"E62")])],"isStart":false});
            var sketch = newSketch(context, id + "F31", { "sketchPlane" : qUnion([Q0])});
            skCircle(sketch, "E63", {"center": v(24, -3) * mm, "radius": 3.1 * mm});
            skSolve(sketch);
        }
        {
            var Q0;
            Q0=qSketchRegion(id+"F31",true);
            extrude(context, id + "F32", {"entities" : qUnion([Q0]), "operationType" : NewBodyOperationType.REMOVE, "oppositeDirection" : true, "depth" : 25 * mm});
        }
        {
            var Q0;
            Q0=makeQuery(id+"F25.opExtrude","SWEPT_FACE",FACE,{"disambiguationData":[OSD([sQuery(id+"F24.wireOp",EDGE,"E51.MirrorCS"),sQuery(id+"F24.wireOp",EDGE,"E57.MirrorCS")])]});
            var sketch = newSketch(context, id + "F33", { "sketchPlane" : qUnion([Q0])});
            skLineSegment(sketch, "E64.bottom", {"start": v(42.3, 13.8) * mm, "end": v(-61.96, 13.8) * mm});
            skLineSegment(sketch, "E64.top", {"start": v(42.3, 8.5) * mm, "end": v(-61.96, 8.5) * mm});
            skLineSegment(sketch, "E64.left", {"start": v(42.3, 13.8) * mm, "end": v(42.3, 8.5) * mm});
            skLineSegment(sketch, "E64.right", {"start": v(-61.96, 13.8) * mm, "end": v(-61.96, 8.5) * mm});
            skSolve(sketch);
        }
        {
            var Q0;
            Q0=qSketchRegion(id+"F33",true);
            extrude(context, id + "F34", {"entities" : qUnion([Q0]), "operationType" : NewBodyOperationType.REMOVE, "oppositeDirection" : true, "depth" : 25 * mm});
        }
        {
            var Q0;
            Q0=makeQuery(id+"F1.opExtrude","CAP_FACE",FACE,{"disambiguationData":[OSD([sQuery(id+"F0.wireOp",EDGE,"E3.bottom"),sQuery(id+"F0.wireOp",EDGE,"E3.top"),sQuery(id+"F0.wireOp",EDGE,"E3.left"),sQuery(id+"F0.wireOp",EDGE,"E3.right"),sQuery(id+"F0.wireOp",EDGE,"E4.left"),sQuery(id+"F0.wireOp",EDGE,"E4.right"),sQuery(id+"F0.wireOp",EDGE,"E5.left"),sQuery(id+"F0.wireOp",EDGE,"E5.right"),sQuery(id+"F0.wireOp",EDGE,"E6.bottom"),sQuery(id+"F0.wireOp",EDGE,"E6.top"),sQuery(id+"F0.wireOp",EDGE,"E7.trimOffspring"),sQuery(id+"F0.wireOp",EDGE,"E8.trimOffspring"),sQuery(id+"F0.wireOp",EDGE,"E9.trimOffspring"),sQuery(id+"F0.wireOp",EDGE,"E10.trimOffspring"),sQuery(id+"F0.wireOp",EDGE,"E11.trimOffspring"),sQuery(id+"F0.wireOp",EDGE,"E12.trimOffspring"),sQuery(id+"F0.wireOp",EDGE,"E13.trimOffspring"),sQuery(id+"F0.wireOp",EDGE,"E14.trimOffspring"),sQuery(id+"F0.wireOp",EDGE,"E15.trimOffspring"),sQuery(id+"F0.wireOp",EDGE,"E17.bottom"),sQuery(id+"F0.wireOp",EDGE,"E17.top"),sQuery(id+"F0.wireOp",EDGE,"E17.left"),sQuery(id+"F0.wireOp",EDGE,"E17.right"),sQuery(id+"F0.wireOp",EDGE,"E18.bottom"),sQuery(id+"F0.wireOp",EDGE,"E18.top"),sQuery(id+"F0.wireOp",EDGE,"E18.left"),sQuery(id+"F0.wireOp",EDGE,"E18.right"),sQuery(id+"F0.wireOp",EDGE,"E19"),sQuery(id+"F0.wireOp",EDGE,"E20"),sQuery(id+"F0.wireOp",EDGE,"E21.bottom"),sQuery(id+"F0.wireOp",EDGE,"E21.top"),sQuery(id+"F0.wireOp",EDGE,"E21.left"),sQuery(id+"F0.wireOp",EDGE,"E21.right")])],"isStart":false});
            var sketch = newSketch(context, id + "F35", { "sketchPlane" : qUnion([Q0])});
            skLineSegment(sketch, "E65.bottom", {"start": v(-9.5, 8.5) * mm, "end": v(9.5, 8.5) * mm});
            skLineSegment(sketch, "E65.top", {"start": v(-9.5, -13.8) * mm, "end": v(9.5, -13.8) * mm});
            skLineSegment(sketch, "E65.left", {"start": v(-9.5, 8.5) * mm, "end": v(-9.5, -13.8) * mm});
            skLineSegment(sketch, "E65.right", {"start": v(9.5, 8.5) * mm, "end": v(9.5, -13.8) * mm});
            skSolve(sketch);
        }
        {
            var Q0;
            Q0=qSketchRegion(id+"F35",true);
            extrude(context, id + "F36", {"entities" : qUnion([Q0]), "operationType" : NewBodyOperationType.ADD, "depth" : 3 * mm});
        }
        {
            var Q0;
            Q0=qSketchRegion(id+"F35",true);
            extrude(context, id + "F37", {"entities" : qUnion([Q0]), "operationType" : NewBodyOperationType.ADD, "depth" : 3 * mm});
        }
        {
            var Q0;
            Q0=makeQuery(id+"F36.boolean.opBoolean","MERGE",FACE,{"derivedFrom":[makeQuery(id+"F25.boolean.opBoolean","MERGE",FACE,{"derivedFrom":[makeQuery(id+"F1.opExtrude","SWEPT_FACE",FACE,{"disambiguationData":[OSD([sQuery(id+"F0.wireOp",EDGE,"E21.bottom")])]}),makeQuery(id+"F25.opExtrude","CAP_FACE",FACE,{"disambiguationData":[OSD([sQuery(id+"F24.wireOp",EDGE,"E48.bottom"),sQuery(id+"F24.wireOp",EDGE,"E48.left"),sQuery(id+"F24.wireOp",EDGE,"E48.right"),sQuery(id+"F24.wireOp",EDGE,"E49.bottom"),sQuery(id+"F24.wireOp",EDGE,"E49.top"),sQuery(id+"F24.wireOp",EDGE,"E49.right")])],"isStart":true}),makeQuery(id+"F25.opExtrude","CAP_FACE",FACE,{"disambiguationData":[OSD([sQuery(id+"F24.wireOp",EDGE,"E51.MirrorCS"),sQuery(id+"F24.wireOp",EDGE,"E53.MirrorCS"),sQuery(id+"F24.wireOp",EDGE,"E54.MirrorCS"),sQuery(id+"F24.wireOp",EDGE,"E55.MirrorCS"),sQuery(id+"F24.wireOp",EDGE,"E56.MirrorCS"),sQuery(id+"F24.wireOp",EDGE,"E57.MirrorCS"),sQuery(id+"F24.wireOp",EDGE,"E58.MirrorCS")])],"isStart":true})]}),makeQuery(id+"F36.opExtrude","SWEPT_FACE",FACE,{"disambiguationData":[OSD([sQuery(id+"F35.wireOp",EDGE,"E65.top")])]})]});
            var sketch = newSketch(context, id + "F38", { "sketchPlane" : qUnion([Q0])});
            skLineSegment(sketch, "E66.bottom", {"start": v(-7.5, 0) * mm, "end": v(7.5, 0) * mm});
            skLineSegment(sketch, "E66.top", {"start": v(-7.5, 2.5) * mm, "end": v(7.5, 2.5) * mm});
            skLineSegment(sketch, "E66.left", {"start": v(-7.5, 0) * mm, "end": v(-7.5, 2.5) * mm});
            skLineSegment(sketch, "E66.right", {"start": v(7.5, 0) * mm, "end": v(7.5, 2.5) * mm});
            skSolve(sketch);
        }
        {
            var Q0;
            Q0=qSketchRegion(id+"F38",true);
            extrude(context, id + "F39", {"entities" : qUnion([Q0]), "operationType" : NewBodyOperationType.REMOVE, "oppositeDirection" : true, "depth" : 30.4 * mm});
        }
        {
            var Q0;
            Q0=sQuery(id+"F0.wireOp",VERTEX,"E23.center");
            var Q1;
            Q1=makeQuery(id+"F1.opExtrude","SWEPT_BODY",BODY,{"disambiguationData":[OSD([sQuery(id+"F0.wireOp",EDGE,"E3.bottom"),sQuery(id+"F0.wireOp",EDGE,"E3.top"),sQuery(id+"F0.wireOp",EDGE,"E3.left"),sQuery(id+"F0.wireOp",EDGE,"E3.right"),sQuery(id+"F0.wireOp",EDGE,"E4.left"),sQuery(id+"F0.wireOp",EDGE,"E4.right"),sQuery(id+"F0.wireOp",EDGE,"E5.left"),sQuery(id+"F0.wireOp",EDGE,"E5.right"),sQuery(id+"F0.wireOp",EDGE,"E6.bottom"),sQuery(id+"F0.wireOp",EDGE,"E6.top"),sQuery(id+"F0.wireOp",EDGE,"E7.trimOffspring"),sQuery(id+"F0.wireOp",EDGE,"E8.trimOffspring"),sQuery(id+"F0.wireOp",EDGE,"E9.trimOffspring"),sQuery(id+"F0.wireOp",EDGE,"E10.trimOffspring"),sQuery(id+"F0.wireOp",EDGE,"E11.trimOffspring"),sQuery(id+"F0.wireOp",EDGE,"E12.trimOffspring"),sQuery(id+"F0.wireOp",EDGE,"E13.trimOffspring"),sQuery(id+"F0.wireOp",EDGE,"E14.trimOffspring"),sQuery(id+"F0.wireOp",EDGE,"E15.trimOffspring"),sQuery(id+"F0.wireOp",EDGE,"E17.bottom"),sQuery(id+"F0.wireOp",EDGE,"E17.top"),sQuery(id+"F0.wireOp",EDGE,"E17.left"),sQuery(id+"F0.wireOp",EDGE,"E17.right"),sQuery(id+"F0.wireOp",EDGE,"E18.bottom"),sQuery(id+"F0.wireOp",EDGE,"E18.top"),sQuery(id+"F0.wireOp",EDGE,"E18.left"),sQuery(id+"F0.wireOp",EDGE,"E18.right"),sQuery(id+"F0.wireOp",EDGE,"E19"),sQuery(id+"F0.wireOp",EDGE,"E20"),sQuery(id+"F0.wireOp",EDGE,"E21.bottom"),sQuery(id+"F0.wireOp",EDGE,"E21.top"),sQuery(id+"F0.wireOp",EDGE,"E21.left"),sQuery(id+"F0.wireOp",EDGE,"E21.right")])]});
            hole(context, id + "F40", {"style" : HoleStyle.SIMPLE, "endStyle" : HoleEndStyle.BLIND, "oppositeDirection" : true, "holeDiameter" : 12.2 * mm, "holeDepth" : 5 * mm, "tappedDepth" : 12 * mm, "tapClearance" : 3, "locations" : qUnion([Q0]), "scope" : qUnion([Q1])});
        }
        {
            var Q0;
            Q0=makeQuery(id+"F30.opExtrude","CAP_FACE",FACE,{"disambiguationData":[OSD([sQuery(id+"F29.wireOp",EDGE,"E62")])],"isStart":false});
            var sketch = newSketch(context, id + "F41", { "sketchPlane" : qUnion([Q0])});
            skCircle(sketch, "E67", {"center": v(24, -3) * mm, "radius": 3.75 * mm});
            skSolve(sketch);
        }
        {
            var Q0;
            Q0=qSketchRegion(id+"F41",true);
            extrude(context, id + "F42", {"entities" : qUnion([Q0]), "operationType" : NewBodyOperationType.REMOVE, "oppositeDirection" : true, "depth" : 1 * mm});
        }
    });
